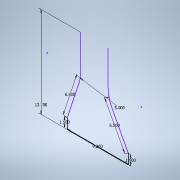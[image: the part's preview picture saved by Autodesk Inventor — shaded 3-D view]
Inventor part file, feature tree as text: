
AUTODESK INVENTOR PART (.ipt)
format: ipt  version: 2021.1 (Build 251245000, 245)  size: 102,912 bytes
history: native  units: in
note: dims shown in document units (in); Inventor stores cm internally (conversion verified against a paired STEP export)
features: sketch x2
ambient origin geometry x8: Origin, YZ Plane, XZ Plane, XY Plane, X Axis, Y Axis, Z Axis, Center Point
feature tree (2):
  sketch  "Sketch1"  dims[d0=9.2in]
  sketch  "Sketch2"  dims[d1=1.5in d2=1.5in d3=6.5in d4=6.5in d5=13.7in d6=5.0in]
